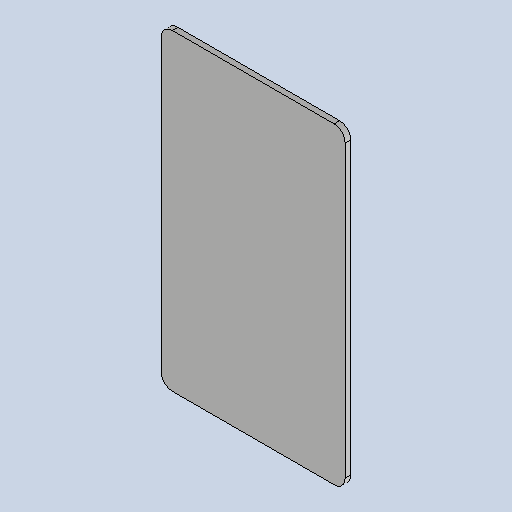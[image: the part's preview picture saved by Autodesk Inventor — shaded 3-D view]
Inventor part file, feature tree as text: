
AUTODESK INVENTOR PART (.ipt)
format: ipt  version: 2025 (Build 290162010, 162A)  size: 97,792 bytes
history: native  units: mm
features: sheet_metal_op x1, chamfer x1, sketch x1, other x1
ambient origin geometry x8: Origin, YZ Plane, XZ Plane, XY Plane, X Axis, Y Axis, Z Axis, Center Point
bodies: Solid1 (feature_tree)
feature tree (4):
  sheet_metal_op  "Face1"
  chamfer  "Corner Round1"
  sketch  "Sketch1"  dims[d0=100.0mm d1=170.0mm d2=3.0mm d3=6.0mm]
  other  "Plate1"
